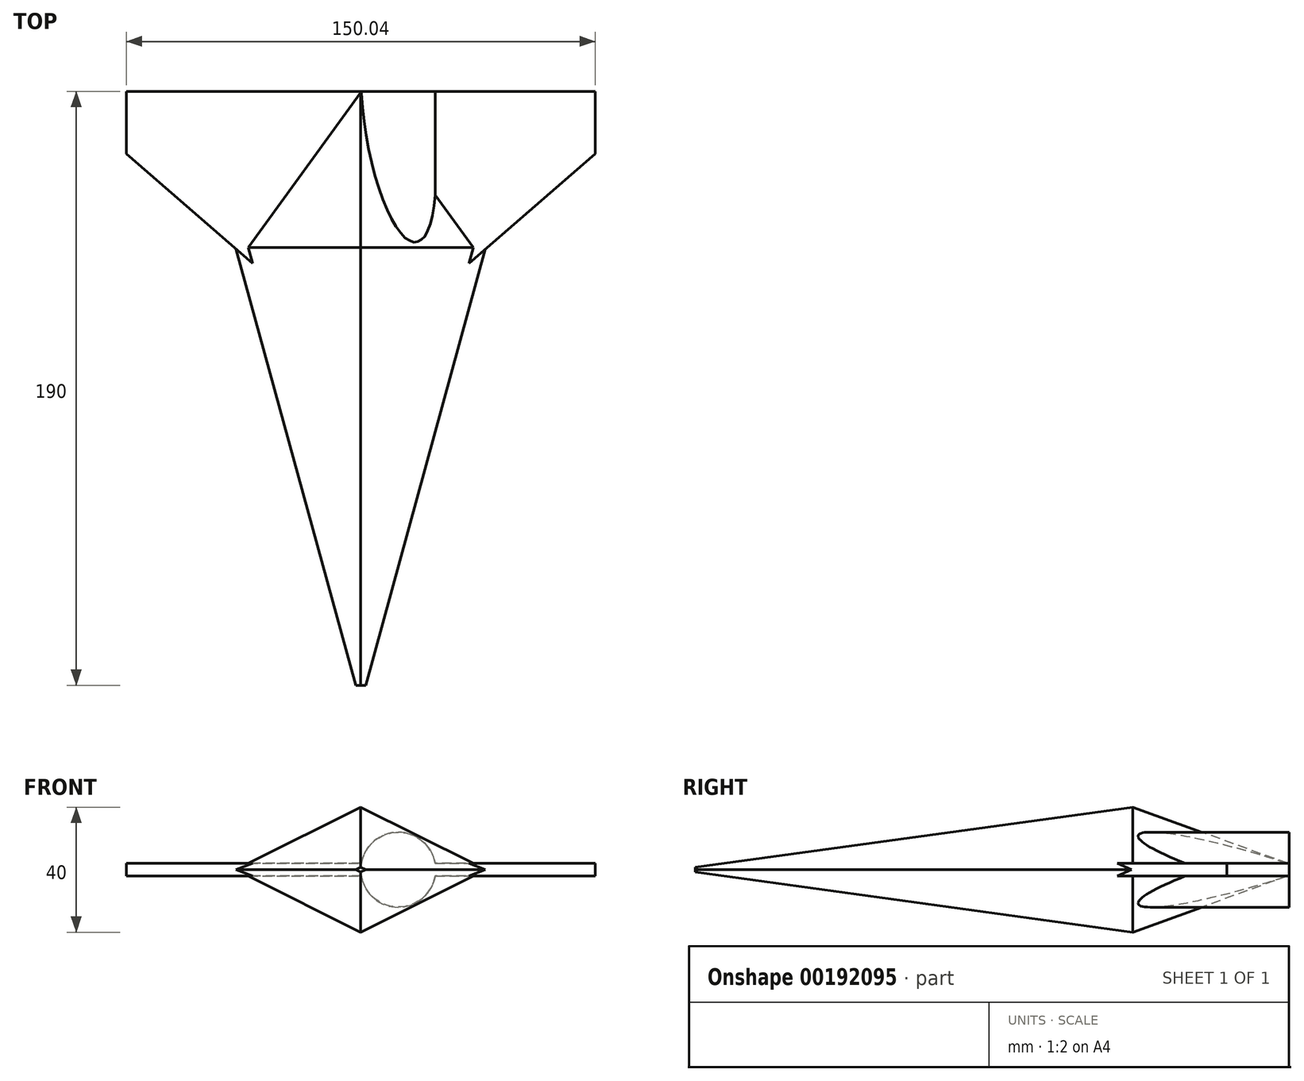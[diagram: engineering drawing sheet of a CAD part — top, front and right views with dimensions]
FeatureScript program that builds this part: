
annotation { "Feature Type Name" : "Feature", "Feature Type Description" : "" }
export const myFeature = defineFeature(function(context is Context, id is Id, definition is map)
    precondition{}
    {
        {
            var Q0;
            Q0=qCreatedBy(makeId("Front.planeOp"),FACE);
            var sketch = newSketch(context, id + "F0", { "sketchPlane" : qUnion([Q0])});
            skLineSegment(sketch, "E0", {"start": v(-40, 0) * mm, "end": v(0, 20) * mm});
            skLineSegment(sketch, "E1.MirrorCS", {"start": v(-40, 0) * mm, "end": v(0, -20) * mm});
            skLineSegment(sketch, "E2.MirrorCS", {"start": v(40, 0) * mm, "end": v(0, 20) * mm});
            skLineSegment(sketch, "E3.MirrorCS", {"start": v(40, 0) * mm, "end": v(0, -20) * mm});
            skSolve(sketch);
        }
        {
            var Q0;
            Q0=makeQuery(id+"F0.imprint","IMPRINT",FACE,{"disambiguationData":[TD([[makeQuery(id+"F0.imprint","IMPRINT",EDGE,{"derivedFrom":sQuery(id+"F0.wireOp",EDGE,"E0")}),-1.0]])]});
            extrude(context, id + "F1", {"entities" : qUnion([Q0]), "depth" : 140 * mm, "hasDraft" : true, "draftAngle" : 7 * degree, "draftPullDirection" : true, "hasSecondDirection" : true, "secondDirectionOppositeDirection" : true, "secondDirectionDepth" : 50 * mm, "hasSecondDirectionDraft" : true, "secondDirectionDraftAngle" : 18 * degree, "secondDirectionDraftPullDirection" : true});
        }
        {
            var Q0;
            Q0=qCreatedBy(makeId("Top.planeOp"),FACE);
            var sketch = newSketch(context, id + "F2", { "sketchPlane" : qUnion([Q0])});
            skLineSegment(sketch, "E4", {"start": v(0, -35) * mm, "end": v(75.02, 30) * mm});
            skLineSegment(sketch, "E5", {"start": v(75.02, 30) * mm, "end": v(75.02, 50) * mm});
            skLineSegment(sketch, "E6", {"start": v(75.02, 50) * mm, "end": v(0, 50) * mm});
            skLineSegment(sketch, "E7", {"start": v(0, 50) * mm, "end": v(0, -35) * mm});
            skLineSegment(sketch, "E8.MirrorCS", {"start": v(0, -35) * mm, "end": v(-75.02, 30) * mm});
            skLineSegment(sketch, "E9.MirrorCS", {"start": v(-75.02, 50) * mm, "end": v(0, 50) * mm});
            skLineSegment(sketch, "E10.MirrorCS", {"start": v(-75.02, 30) * mm, "end": v(-75.02, 50) * mm});
            skSolve(sketch);
        }
        {
            var Q0;
            Q0 = qSketchRegion(id + "F2", true);
            extrude(context, id + "F3", {"entities" : qUnion([Q0]), "operationType" : NewBodyOperationType.ADD, "endBound" : BoundingType.SYMMETRIC, "depth" : 4 * mm});
        }
        {
            var Q0;
            Q0=qCreatedBy(makeId("Front.planeOp"),FACE);
            var sketch = newSketch(context, id + "F4", { "sketchPlane" : qUnion([Q0])});
            skCircle(sketch, "E11", {"center": v(12, 0) * mm, "radius": 12 * mm});
            skCircle(sketch, "E12.MirrorC", {"center": v(-12, 0) * mm, "radius": 12 * mm});
            skSolve(sketch);
        }
        {
            var Q0;
            Q0=makeQuery(id+"F4.imprint","IMPRINT",FACE,{"disambiguationData":[TD([[makeQuery(id+"F4.imprint","IMPRINT",EDGE,{"derivedFrom":sQuery(id+"F4.wireOp",EDGE,"E11")}),1.0]])]});
            var Q1;
            Q1=makeQuery(id+"F4.imprint","IMPRINT",FACE,{"disambiguationData":[TD([[makeQuery(id+"F4.imprint","IMPRINT",EDGE,{"derivedFrom":sQuery(id+"F4.wireOp",EDGE,"E12.MirrorC")}),-1.0]])]});
            extrude(context, id + "F5", {"entities" : qUnion([Q0, Q1]), "operationType" : NewBodyOperationType.ADD, "oppositeDirection" : true, "depth" : 50 * mm});
        }
    });
